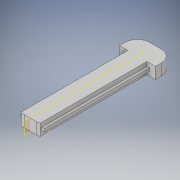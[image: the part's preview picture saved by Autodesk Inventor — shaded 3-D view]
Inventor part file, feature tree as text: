
AUTODESK INVENTOR PART (.ipt)
format: ipt  version: 2018 (Build 220112000, 112)  size: 181,248 bytes
history: native  units: in
note: dims shown in document units (in); Inventor stores cm internally (conversion verified against a paired STEP export)
features: sketch x7, extrude x6, mirror x3, fillet x2, plane x1
ambient origin geometry x8: Origin, YZ Plane, XZ Plane, XY Plane, X Axis, Y Axis, Z Axis, Center Point
bodies: Solid1 (feature_tree)
feature tree (19):
  extrude  "Extrusion1"  Depth=2.25in
  sketch  "Sketch2"  dims[d2=0.24in d3=0.0in d4=0.06in]
  extrude  "Extrusion2"  Depth=0.06in
  plane  "Work Plane1"
  mirror  "Mirror1"
  extrude  "Extrusion3"  Depth=0.09in
  fillet  "Fillet2"  Radius=0.0525in
  extrude  "Extrusion4"  Depth=0.24in
  mirror  "Mirror2"
  extrude  "Extrusion5"  Depth=0.375in
  mirror  "Mirror3"
  extrude  "Extrusion6"  Depth=0.25in
  fillet  "Fillet3"  Radius=0.3in
  sketch  "Sketch1"  dims[d0=0.4in d1=2.25in]
  sketch  "Sketch3"  dims[d5=2.25in d6=0.09in d7=0.0525in d8=0.0in]
  sketch  "Sketch4"  dims[d9=0.25in d10=0.0in d12=0.24in]
  sketch  "Sketch5"  dims[d13=0.75in d14=0.375in]
  sketch  "Sketch6"  dims[d15=0.25in d16=0.25in d17=0.3in d18=0.0in]
  sketch  "Sketch7"  dims[d19=2.2in d20=0.3in d21=0.0in d22=0.75in d23=0.375in d24=0.24in d25=0.0in d26=0.25in]
